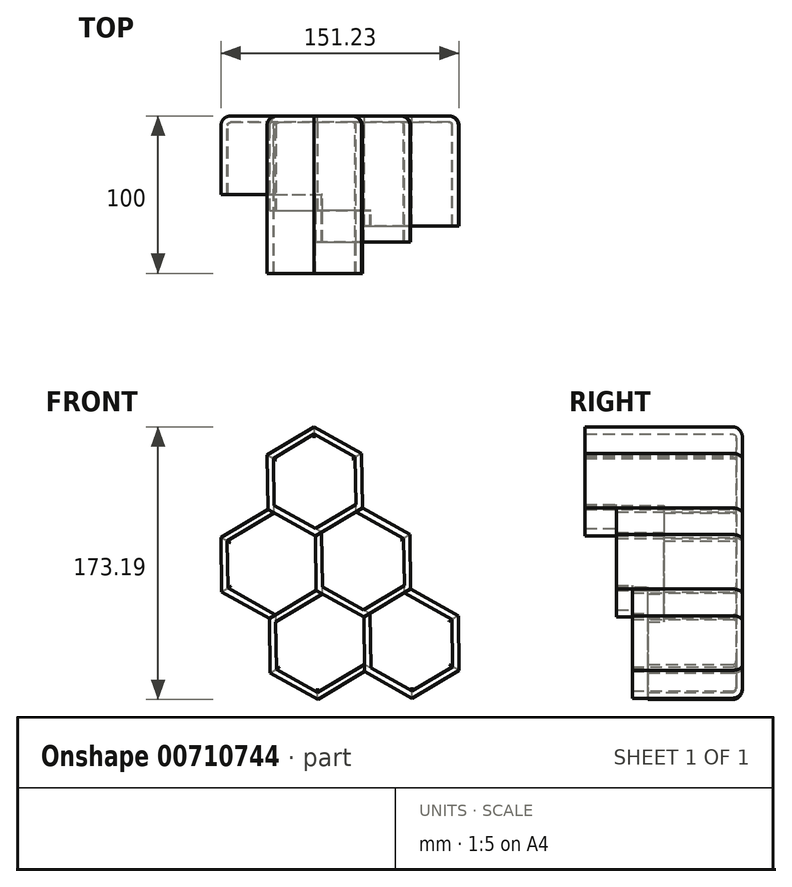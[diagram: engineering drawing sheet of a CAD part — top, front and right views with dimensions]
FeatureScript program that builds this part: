
annotation { "Feature Type Name" : "Feature", "Feature Type Description" : "" }
export const myFeature = defineFeature(function(context is Context, id is Id, definition is map)
    precondition{}
    {
        {
            var Q0;
            Q0=qCreatedBy(makeId("Front.planeOp"),FACE);
            var sketch = newSketch(context, id + "F0", { "sketchPlane" : qUnion([Q0])});
            skCircle(sketch, "E0.cCircle", {"center": v(0, 0) * mm, "radius": 30 * mm, "construction": true});
            skLineSegment(sketch, "E0.0", {"start": v(-0.5, 34.64) * mm, "end": v(29.75, 17.75) * mm});
            skLineSegment(sketch, "E0.1", {"start": v(29.75, 17.75) * mm, "end": v(30.25, -16.89) * mm});
            skLineSegment(sketch, "E0.2", {"start": v(30.25, -16.89) * mm, "end": v(0.5, -34.64) * mm});
            skLineSegment(sketch, "E0.3", {"start": v(0.5, -34.64) * mm, "end": v(-29.75, -17.75) * mm});
            skLineSegment(sketch, "E0.4", {"start": v(-29.75, -17.75) * mm, "end": v(-30.25, 16.89) * mm});
            skLineSegment(sketch, "E0.5", {"start": v(-30.25, 16.89) * mm, "end": v(-0.5, 34.64) * mm});
            skPoint(sketch, "E0.0.midPoint", {"position": v(14.63, 26.2) * mm});
            skLineSegment(sketch, "E1.MirrorCS", {"start": v(-60.5, 33.78) * mm, "end": v(-30.25, 16.89) * mm});
            skLineSegment(sketch, "E2.MirrorCS", {"start": v(-61, 68.41) * mm, "end": v(-60.5, 33.78) * mm});
            skLineSegment(sketch, "E3.MirrorCS", {"start": v(-31.24, 86.16) * mm, "end": v(-61, 68.41) * mm});
            skLineSegment(sketch, "E4.MirrorCS", {"start": v(-1, 69.28) * mm, "end": v(-31.24, 86.16) * mm});
            skLineSegment(sketch, "E5.MirrorCS", {"start": v(-0.5, 34.64) * mm, "end": v(-1, 69.28) * mm});
            skCircle(sketch, "E6.MirrorC", {"center": v(-60, -0.86) * mm, "radius": 30 * mm, "construction": true});
            skLineSegment(sketch, "E7.MirrorCS", {"start": v(-59.5, -35.5) * mm, "end": v(-29.75, -17.75) * mm});
            skLineSegment(sketch, "E8.MirrorCS", {"start": v(-89.74, -18.61) * mm, "end": v(-59.5, -35.5) * mm});
            skLineSegment(sketch, "E9.MirrorCS", {"start": v(-90.24, 16.03) * mm, "end": v(-89.74, -18.61) * mm});
            skLineSegment(sketch, "E10.MirrorCS", {"start": v(-60.5, 33.78) * mm, "end": v(-90.24, 16.03) * mm});
            skLineSegment(sketch, "E11.MirrorCS", {"start": v(1, -69.28) * mm, "end": v(0.5, -34.64) * mm});
            skLineSegment(sketch, "E12.MirrorCS", {"start": v(-28.75, -87.03) * mm, "end": v(1, -69.28) * mm});
            skLineSegment(sketch, "E13.MirrorCS", {"start": v(-59, -70.14) * mm, "end": v(-28.75, -87.03) * mm});
            skLineSegment(sketch, "E14.MirrorCS", {"start": v(-59.5, -35.5) * mm, "end": v(-59, -70.14) * mm});
            skLineSegment(sketch, "E15.MirrorCS", {"start": v(-29.75, -17.75) * mm, "end": v(0.5, -34.64) * mm});
            skLineSegment(sketch, "E16.MirrorCS", {"start": v(-59, -70.14) * mm, "end": v(-59.5, -35.5) * mm});
            skLineSegment(sketch, "E17.MirrorCS", {"start": v(-28.75, -87.03) * mm, "end": v(-59, -70.14) * mm});
            skLineSegment(sketch, "E18.MirrorCS", {"start": v(1, -69.28) * mm, "end": v(31.24, -86.16) * mm});
            skLineSegment(sketch, "E19.MirrorCS", {"start": v(31.24, -86.16) * mm, "end": v(61, -68.41) * mm});
            skLineSegment(sketch, "E20.MirrorCS", {"start": v(61, -68.41) * mm, "end": v(60.5, -33.78) * mm});
            skLineSegment(sketch, "E21.MirrorCS", {"start": v(60.5, -33.78) * mm, "end": v(30.25, -16.89) * mm});
            skSolve(sketch);
        }
        {
            var Q0;
            Q0=makeQuery(id+"F0.imprint","IMPRINT",FACE,{"disambiguationData":[TD([[makeQuery(id+"F0.imprint","IMPRINT",EDGE,{"derivedFrom":sQuery(id+"F0.wireOp",EDGE,"E0.5")}),1.0]])]});
            extrude(context, id + "F1", {"entities" : qUnion([Q0]), "depth" : 100 * mm, "offsetDistance" : 25 * mm});
        }
        {
            var Q0;
            Q0=makeQuery(id+"F0.imprint","IMPRINT",FACE,{"disambiguationData":[TD([[makeQuery(id+"F0.imprint","IMPRINT",EDGE,{"derivedFrom":sQuery(id+"F0.wireOp",EDGE,"E0.0")}),-1.0]])]});
            extrude(context, id + "F2", {"entities" : qUnion([Q0]), "operationType" : NewBodyOperationType.ADD, "depth" : 80 * mm, "offsetDistance" : 25 * mm});
        }
        {
            var Q0;
            Q0=makeQuery(id+"F0.imprint","IMPRINT",FACE,{"disambiguationData":[TD([[makeQuery(id+"F0.imprint","IMPRINT",EDGE,{"derivedFrom":sQuery(id+"F0.wireOp",EDGE,"E0.2")}),1.0]])]});
            extrude(context, id + "F3", {"entities" : qUnion([Q0]), "operationType" : NewBodyOperationType.ADD, "depth" : 70 * mm, "offsetDistance" : 25 * mm});
        }
        {
            var Q0;
            Q0=makeQuery(id+"F0.imprint","IMPRINT",FACE,{"disambiguationData":[TD([[makeQuery(id+"F0.imprint","IMPRINT",EDGE,{"derivedFrom":sQuery(id+"F0.wireOp",EDGE,"E0.4")}),1.0]])]});
            extrude(context, id + "F4", {"entities" : qUnion([Q0]), "operationType" : NewBodyOperationType.ADD, "depth" : 50 * mm, "offsetDistance" : 25 * mm});
        }
        {
            var Q0;
            Q0=makeQuery(id+"F0.imprint","IMPRINT",FACE,{"disambiguationData":[TD([[makeQuery(id+"F0.imprint","IMPRINT",EDGE,{"derivedFrom":sQuery(id+"F0.wireOp",EDGE,"E12.MirrorCS")}),1.0]])]});
            extrude(context, id + "F5", {"entities" : qUnion([Q0]), "operationType" : NewBodyOperationType.ADD, "depth" : 60 * mm, "offsetDistance" : 25 * mm});
        }
        {
            var Q0;
            {var subQ0=sQuery(id+"F0.wireOp",EDGE,"E11.MirrorCS");var subQ1=sQuery(id+"F0.wireOp",EDGE,"E7.MirrorCS");var subQ2=sQuery(id+"F0.wireOp",EDGE,"E15.MirrorCS");var subQ3=sQuery(id+"F0.wireOp",EDGE,"E1.MirrorCS");var subQ4=sQuery(id+"F0.wireOp",EDGE,"E0.4");var subQ5=sQuery(id+"F0.wireOp",EDGE,"E0.2");var subQ6=sQuery(id+"F0.wireOp",EDGE,"E0.5");Q0=makeQuery(id+"F5.boolean.opBoolean","MERGE",FACE,{"derivedFrom":[makeQuery(id+"F4.boolean.opBoolean","MERGE",FACE,{"derivedFrom":[makeQuery(id+"F3.boolean.opBoolean","MERGE",FACE,{"derivedFrom":[makeQuery(id+"F2.boolean.opBoolean","MERGE",FACE,{"derivedFrom":[makeQuery(id+"F1.opExtrude","CAP_FACE",FACE,{"disambiguationData":[OSD([subQ6,subQ3,sQuery(id+"F0.wireOp",EDGE,"E2.MirrorCS"),sQuery(id+"F0.wireOp",EDGE,"E3.MirrorCS"),sQuery(id+"F0.wireOp",EDGE,"E4.MirrorCS"),sQuery(id+"F0.wireOp",EDGE,"E5.MirrorCS")])],"isStart":true}),makeQuery(id+"F2.opExtrude","CAP_FACE",FACE,{"disambiguationData":[OSD([sQuery(id+"F0.wireOp",EDGE,"E0.0"),sQuery(id+"F0.wireOp",EDGE,"E0.1"),subQ5,subQ4,subQ6,subQ2])],"isStart":true})]}),makeQuery(id+"F3.opExtrude","CAP_FACE",FACE,{"disambiguationData":[OSD([subQ5,subQ0,sQuery(id+"F0.wireOp",EDGE,"E18.MirrorCS"),sQuery(id+"F0.wireOp",EDGE,"E19.MirrorCS"),sQuery(id+"F0.wireOp",EDGE,"E20.MirrorCS"),sQuery(id+"F0.wireOp",EDGE,"E21.MirrorCS")])],"isStart":true})]}),makeQuery(id+"F4.opExtrude","CAP_FACE",FACE,{"disambiguationData":[OSD([subQ4,subQ3,sQuery(id+"F0.wireOp",EDGE,"E8.MirrorCS"),sQuery(id+"F0.wireOp",EDGE,"E9.MirrorCS"),sQuery(id+"F0.wireOp",EDGE,"E10.MirrorCS"),subQ1])],"isStart":true})]}),makeQuery(id+"F5.opExtrude","CAP_FACE",FACE,{"disambiguationData":[OSD([sQuery(id+"F0.wireOp",EDGE,"E12.MirrorCS"),subQ2,subQ1,sQuery(id+"F0.wireOp",EDGE,"E16.MirrorCS"),sQuery(id+"F0.wireOp",EDGE,"E17.MirrorCS"),subQ0])],"isStart":true})]});}
            fillet(context, id + "F6", {"entities" : qUnion([Q0]), "radius" : 6 * mm, "tangentPropagation" : true, "allowEdgeOverflow" : false});
        }
        {
            var Q0;
            Q0=makeQuery(id+"F1.opExtrude","CAP_FACE",FACE,{"disambiguationData":[OSD([sQuery(id+"F0.wireOp",EDGE,"E0.5"),sQuery(id+"F0.wireOp",EDGE,"E1.MirrorCS"),sQuery(id+"F0.wireOp",EDGE,"E2.MirrorCS"),sQuery(id+"F0.wireOp",EDGE,"E3.MirrorCS"),sQuery(id+"F0.wireOp",EDGE,"E4.MirrorCS"),sQuery(id+"F0.wireOp",EDGE,"E5.MirrorCS")])],"isStart":false});
            var Q1;
            Q1=makeQuery(id+"F4.opExtrude","CAP_FACE",FACE,{"disambiguationData":[OSD([sQuery(id+"F0.wireOp",EDGE,"E0.4"),sQuery(id+"F0.wireOp",EDGE,"E1.MirrorCS"),sQuery(id+"F0.wireOp",EDGE,"E8.MirrorCS"),sQuery(id+"F0.wireOp",EDGE,"E9.MirrorCS"),sQuery(id+"F0.wireOp",EDGE,"E10.MirrorCS"),sQuery(id+"F0.wireOp",EDGE,"E7.MirrorCS")])],"isStart":false});
            var Q2;
            Q2=makeQuery(id+"F2.opExtrude","CAP_FACE",FACE,{"disambiguationData":[OSD([sQuery(id+"F0.wireOp",EDGE,"E0.0"),sQuery(id+"F0.wireOp",EDGE,"E0.1"),sQuery(id+"F0.wireOp",EDGE,"E0.2"),sQuery(id+"F0.wireOp",EDGE,"E0.4"),sQuery(id+"F0.wireOp",EDGE,"E0.5"),sQuery(id+"F0.wireOp",EDGE,"E15.MirrorCS")])],"isStart":false});
            var Q3;
            Q3=makeQuery(id+"F5.opExtrude","CAP_FACE",FACE,{"disambiguationData":[OSD([sQuery(id+"F0.wireOp",EDGE,"E12.MirrorCS"),sQuery(id+"F0.wireOp",EDGE,"E15.MirrorCS"),sQuery(id+"F0.wireOp",EDGE,"E7.MirrorCS"),sQuery(id+"F0.wireOp",EDGE,"E16.MirrorCS"),sQuery(id+"F0.wireOp",EDGE,"E17.MirrorCS"),sQuery(id+"F0.wireOp",EDGE,"E11.MirrorCS")])],"isStart":false});
            var Q4;
            Q4=makeQuery(id+"F3.opExtrude","CAP_FACE",FACE,{"disambiguationData":[OSD([sQuery(id+"F0.wireOp",EDGE,"E0.2"),sQuery(id+"F0.wireOp",EDGE,"E11.MirrorCS"),sQuery(id+"F0.wireOp",EDGE,"E18.MirrorCS"),sQuery(id+"F0.wireOp",EDGE,"E19.MirrorCS"),sQuery(id+"F0.wireOp",EDGE,"E20.MirrorCS"),sQuery(id+"F0.wireOp",EDGE,"E21.MirrorCS")])],"isStart":false});
            shell(context, id + "F7", {"entities" : qUnion([Q0, Q1, Q2, Q3, Q4]), "thickness" : 4 * mm});
        }
    });
